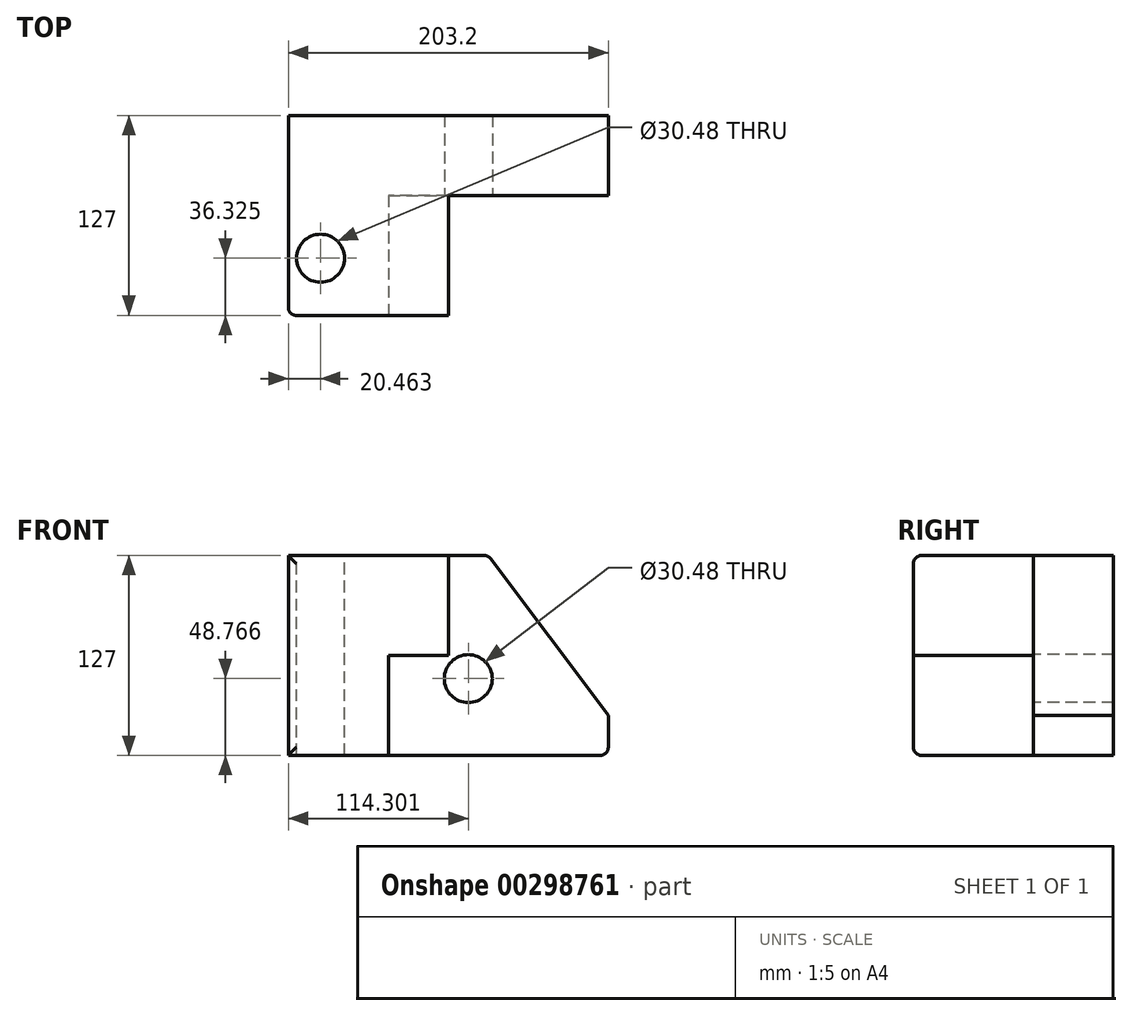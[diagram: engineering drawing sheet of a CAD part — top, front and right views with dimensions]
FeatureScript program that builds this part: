
annotation { "Feature Type Name" : "Feature", "Feature Type Description" : "" }
export const myFeature = defineFeature(function(context is Context, id is Id, definition is map)
    precondition{}
    {
        {
            var Q0;
            Q0=qCreatedBy(makeId("Front.planeOp"),FACE);
            var sketch = newSketch(context, id + "F0", { "sketchPlane" : qUnion([Q0])});
            skLineSegment(sketch, "E0.bottom", {"start": v(-105.8, 57.29) * mm, "end": v(97.4, 57.29) * mm});
            skLineSegment(sketch, "E0.top", {"start": v(-105.8, -69.71) * mm, "end": v(97.4, -69.71) * mm});
            skLineSegment(sketch, "E0.left", {"start": v(-105.8, 57.29) * mm, "end": v(-105.8, -69.71) * mm});
            skLineSegment(sketch, "E0.right", {"start": v(97.4, 57.29) * mm, "end": v(97.4, -69.71) * mm});
            skSolve(sketch);
        }
        {
            var Q0;
            Q0 = qSketchRegion(id + "F0", true);
            extrude(context, id + "F1", {"entities" : qUnion([Q0]), "depth" : 127 * mm});
        }
        {
            var Q0;
            Q0=makeQuery(id+"F1.opExtrude","CAP_FACE",FACE,{"disambiguationData":[OSD([sQuery(id+"F0.wireOp",EDGE,"E0.bottom"),sQuery(id+"F0.wireOp",EDGE,"E0.top"),sQuery(id+"F0.wireOp",EDGE,"E0.left"),sQuery(id+"F0.wireOp",EDGE,"E0.right")])],"isStart":false});
            var sketch = newSketch(context, id + "F2", { "sketchPlane" : qUnion([Q0])});
            skLineSegment(sketch, "E1", {"start": v(-105.8, 57.29) * mm, "end": v(-4.2, 57.29) * mm});
            skLineSegment(sketch, "E2", {"start": v(-4.2, 57.29) * mm, "end": v(-4.2, -6.21) * mm});
            skLineSegment(sketch, "E3", {"start": v(-4.2, -6.21) * mm, "end": v(-42.3, -6.21) * mm});
            skLineSegment(sketch, "E4", {"start": v(-42.3, -6.21) * mm, "end": v(-42.3, -69.71) * mm});
            skLineSegment(sketch, "E5", {"start": v(-42.3, -69.71) * mm, "end": v(-105.8, -69.71) * mm});
            skLineSegment(sketch, "E6", {"start": v(-105.8, -69.71) * mm, "end": v(-105.8, 57.29) * mm});
            skSolve(sketch);
        }
        {
            var Q0;
            {var subQ3=sQuery(id+"F2.wireOp",EDGE,"E2");Q0=makeQuery(id+"F2.imprint","IMPRINT",FACE,{"disambiguationData":[TD([[makeQuery(id+"F2.imprint","IMPRINT",EDGE,{"derivedFrom":subQ3}),1.0]])]});}
            extrude(context, id + "F3", {"entities" : qUnion([Q0]), "operationType" : NewBodyOperationType.REMOVE, "oppositeDirection" : true, "depth" : 76.2 * mm});
        }
        {
            var Q0;
            Q0=makeQuery(id+"F1.opExtrude","SWEPT_EDGE",EDGE,{"disambiguationData":[OSD([sQuery(id+"F0.wireOp",EDGE,"E0.bottom"),sQuery(id+"F0.wireOp",EDGE,"E0.right")])]});
            chamfer(context, id + "F4", {"entities" : qUnion([Q0]), "chamferType" : ChamferType.TWO_OFFSETS, "width1" : 76.2 * mm, "oppositeDirection" : false, "width2" : 101.6 * mm, "tangentPropagation" : true});
        }
        {
            var Q0;
            Q0=makeQuery(id+"F1.opExtrude","CAP_EDGE",EDGE,{"disambiguationData":[OSD([sQuery(id+"F0.wireOp",EDGE,"E0.bottom")])],"isStart":false});
            var Q1;
            Q1=makeQuery(id+"F3.boolean.opBoolean","COPY",EDGE,{"derivedFrom":makeQuery(id+"F3.opExtrude","SWEPT_EDGE",EDGE,{"disambiguationData":[OSD([sQuery(id+"F0.wireOp",EDGE,"E0.bottom"),sQuery(id+"F2.wireOp",EDGE,"E1"),sQuery(id+"F2.wireOp",EDGE,"E2")])]})});
            var Q2;
            Q2=makeQuery(id+"F3.boolean.opBoolean","COPY",EDGE,{"derivedFrom":makeQuery(id+"F3.opExtrude","CAP_EDGE",EDGE,{"disambiguationData":[OSD([sQuery(id+"F0.wireOp",EDGE,"E0.bottom")])],"isStart":false})});
            var Q3;
            {var subQ0=sQuery(id+"F0.wireOp",EDGE,"E0.bottom");Q3=makeQuery(id+"F4.opChamfer","BLEND_EDGE",EDGE,{"blendedFrom":[makeQuery(id+"F1.opExtrude","SWEPT_EDGE",EDGE,{"disambiguationData":[OSD([subQ0,sQuery(id+"F0.wireOp",EDGE,"E0.right")])]}),makeQuery(id+"F1.opExtrude","SWEPT_FACE",FACE,{"disambiguationData":[OSD([subQ0])]})],"blendedInto":[makeQuery(id+"F1.opExtrude","SWEPT_FACE",FACE,{"disambiguationData":[OSD([subQ0])]})]});}
            var Q4;
            Q4=makeQuery(id+"F3.boolean.opBoolean","COPY",EDGE,{"derivedFrom":makeQuery(id+"F3.opExtrude","CAP_EDGE",EDGE,{"disambiguationData":[OSD([sQuery(id+"F2.wireOp",EDGE,"E2")])],"isStart":true})});
            var Q5;
            Q5=makeQuery(id+"F3.boolean.opBoolean","COPY",EDGE,{"derivedFrom":makeQuery(id+"F3.opExtrude","CAP_EDGE",EDGE,{"disambiguationData":[OSD([sQuery(id+"F2.wireOp",EDGE,"E3")])],"isStart":true})});
            var Q6;
            Q6=makeQuery(id+"F3.boolean.opBoolean","COPY",EDGE,{"derivedFrom":makeQuery(id+"F3.opExtrude","CAP_EDGE",EDGE,{"disambiguationData":[OSD([sQuery(id+"F2.wireOp",EDGE,"E4")])],"isStart":true})});
            var Q7;
            Q7=makeQuery(id+"F1.opExtrude","CAP_EDGE",EDGE,{"disambiguationData":[OSD([sQuery(id+"F0.wireOp",EDGE,"E0.top")])],"isStart":false});
            var Q8;
            Q8=makeQuery(id+"F1.opExtrude","CAP_EDGE",EDGE,{"disambiguationData":[OSD([sQuery(id+"F0.wireOp",EDGE,"E0.left")])],"isStart":false});
            var Q9;
            Q9=makeQuery(id+"F3.boolean.opBoolean","COPY",EDGE,{"derivedFrom":makeQuery(id+"F3.opExtrude","SWEPT_EDGE",EDGE,{"disambiguationData":[OSD([sQuery(id+"F0.wireOp",EDGE,"E0.top"),sQuery(id+"F2.wireOp",EDGE,"E4"),sQuery(id+"F2.wireOp",EDGE,"E5")])]})});
            var Q10;
            Q10=makeQuery(id+"F3.boolean.opBoolean","COPY",EDGE,{"derivedFrom":makeQuery(id+"F3.opExtrude","CAP_EDGE",EDGE,{"disambiguationData":[OSD([sQuery(id+"F0.wireOp",EDGE,"E0.top")])],"isStart":false})});
            var Q11;
            Q11=makeQuery(id+"F1.opExtrude","SWEPT_EDGE",EDGE,{"disambiguationData":[OSD([sQuery(id+"F0.wireOp",EDGE,"E0.top"),sQuery(id+"F0.wireOp",EDGE,"E0.right")])]});
            fillet(context, id + "F5", {"entities" : qUnion([Q0, Q1, Q2, Q3, Q4, Q5, Q6, Q7, Q8, Q9, Q10, Q11]), "radius" : 5.08 * mm, "tangentPropagation" : true, "allowEdgeOverflow" : false});
        }
        {
            var Q0;
            Q0=makeQuery(id+"F3.boolean.opBoolean","COPY",FACE,{"derivedFrom":makeQuery(id+"F3.opExtrude","CAP_FACE",FACE,{"disambiguationData":[OSD([sQuery(id+"F0.wireOp",EDGE,"E0.bottom"),sQuery(id+"F0.wireOp",EDGE,"E0.top"),sQuery(id+"F0.wireOp",EDGE,"E0.right"),sQuery(id+"F2.wireOp",EDGE,"E2"),sQuery(id+"F2.wireOp",EDGE,"E3"),sQuery(id+"F2.wireOp",EDGE,"E4")])],"isStart":false})});
            var sketch = newSketch(context, id + "F6", { "sketchPlane" : qUnion([Q0])});
            skCircle(sketch, "E7", {"center": v(8.5, -20.94) * mm, "radius": 15.24 * mm});
            skSolve(sketch);
        }
        {
            var Q0;
            Q0 = qSketchRegion(id + "F6", true);
            extrude(context, id + "F7", {"entities" : qUnion([Q0]), "operationType" : NewBodyOperationType.REMOVE, "oppositeDirection" : true, "depth" : 50.8 * mm});
        }
        {
            var Q0;
            Q0=makeQuery(id+"F1.opExtrude","SWEPT_FACE",FACE,{"disambiguationData":[OSD([sQuery(id+"F0.wireOp",EDGE,"E0.bottom")])]});
            var sketch = newSketch(context, id + "F8", { "sketchPlane" : qUnion([Q0])});
            skCircle(sketch, "E8", {"center": v(-85.35, -90.67) * mm, "radius": 15.24 * mm});
            skSolve(sketch);
        }
        {
            var Q0;
            Q0 = qSketchRegion(id + "F8", true);
            var Q1;
            Q1=makeQuery(id+"F1.opExtrude","SWEPT_BODY",BODY,{"disambiguationData":[OSD([sQuery(id+"F0.wireOp",EDGE,"E0.bottom"),sQuery(id+"F0.wireOp",EDGE,"E0.top"),sQuery(id+"F0.wireOp",EDGE,"E0.left"),sQuery(id+"F0.wireOp",EDGE,"E0.right")])]});
            extrude(context, id + "F9", {"entities" : qUnion([Q0]), "operationType" : NewBodyOperationType.REMOVE, "endBound" : BoundingType.UP_TO_BODY, "oppositeDirection" : true, "endBoundEntityBody" : qUnion([Q1]), "depth" : 25.4 * mm});
        }
    });
